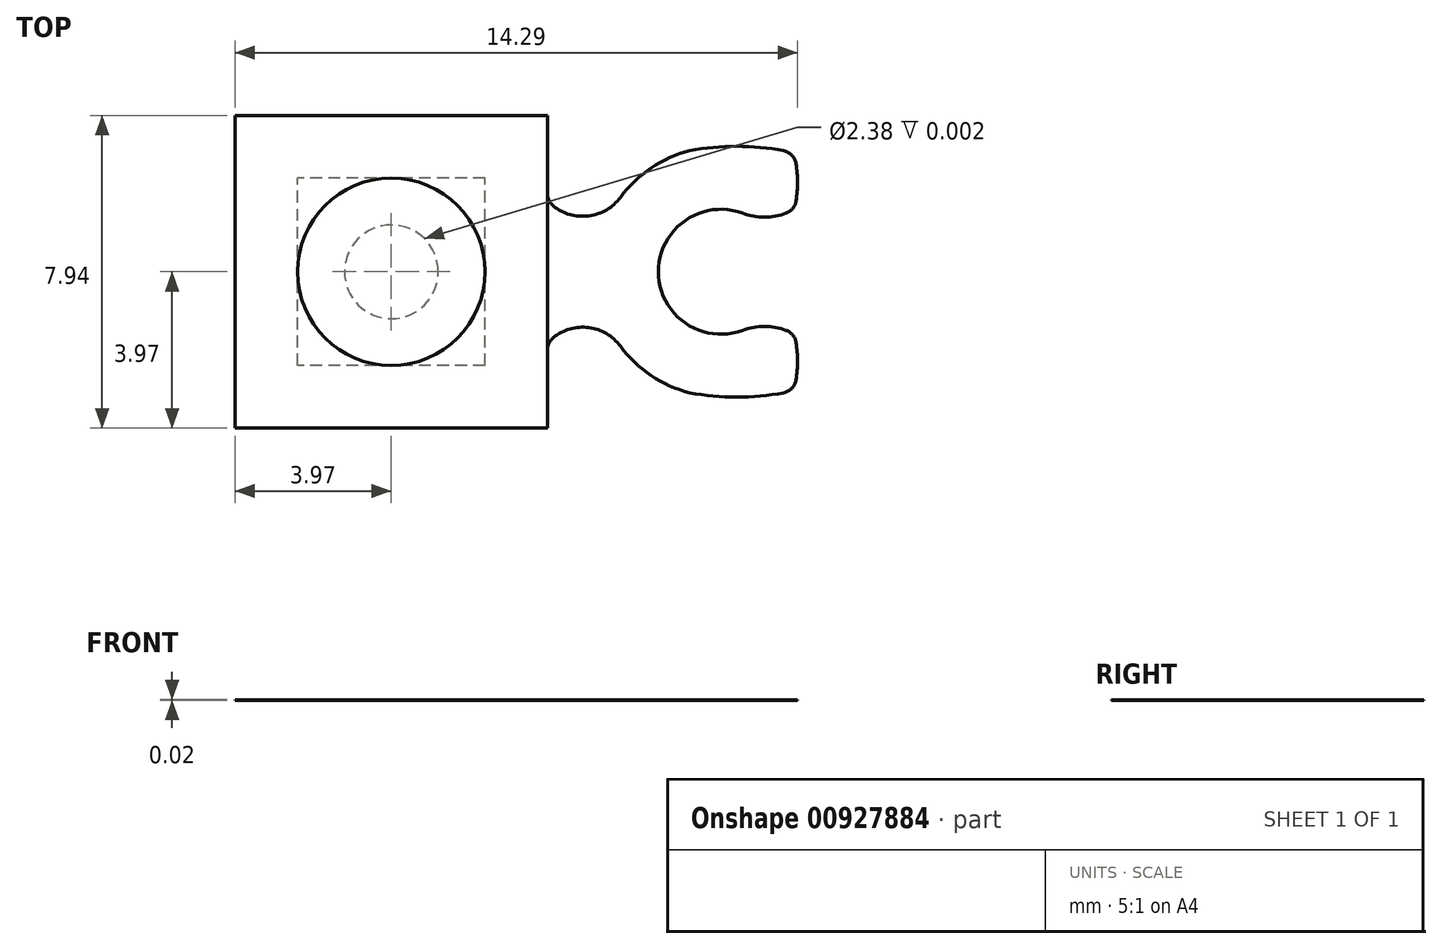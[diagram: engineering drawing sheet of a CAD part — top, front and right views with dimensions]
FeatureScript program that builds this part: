
annotation { "Feature Type Name" : "Feature", "Feature Type Description" : "" }
export const myFeature = defineFeature(function(context is Context, id is Id, definition is map)
    precondition{}
    {
        {
            var Q0;
            Q0=qCreatedBy(makeId("Top.planeOp"),FACE);
            var sketch = newSketch(context, id + "F0", { "sketchPlane" : qUnion([Q0])});
            skLineSegment(sketch, "E0.bottom", {"start": v(3.97, 3.97) * mm, "end": v(-3.97, 3.97) * mm});
            skLineSegment(sketch, "E0.top", {"start": v(3.97, -3.97) * mm, "end": v(-3.97, -3.97) * mm});
            skLineSegment(sketch, "E0.left", {"start": v(3.97, 3.97) * mm, "end": v(3.97, -3.97) * mm});
            skLineSegment(sketch, "E0.right", {"start": v(-3.97, 3.97) * mm, "end": v(-3.97, -3.97) * mm});
            skPoint(sketch, "E0.middle", {"position": v(0, 0) * mm});
            skSolve(sketch);
        }
        {
            var Q0;
            Q0 = qSketchRegion(id + "F0", true);
            extrude(context, id + "F1", {"entities" : qUnion([Q0]), "depth" : 3 / 203.2 * mm, "offsetDistance" : 25.4 * mm});
        }
        {
            var Q0;
            Q0=makeQuery(id+"F1.opExtrude","CAP_FACE",FACE,{"disambiguationData":[OSD([sQuery(id+"F0.wireOp",EDGE,"E0.bottom"),sQuery(id+"F0.wireOp",EDGE,"E0.top"),sQuery(id+"F0.wireOp",EDGE,"E0.left"),sQuery(id+"F0.wireOp",EDGE,"E0.right")])],"isStart":false});
            var sketch = newSketch(context, id + "F2", { "sketchPlane" : qUnion([Q0])});
            skCircle(sketch, "E1", {"center": v(0, 0) * mm, "radius": 2.38 * mm});
            skSolve(sketch);
        }
        {
            var Q0;
            Q0 = qSketchRegion(id + "F2", true);
            extrude(context, id + "F3", {"entities" : qUnion([Q0]), "operationType" : NewBodyOperationType.ADD, "depth" : 1 / 406.4 * mm, "offsetDistance" : 25.4 * mm});
        }
        {
            var Q0;
            Q0=makeQuery(id+"F1.opExtrude","CAP_FACE",FACE,{"disambiguationData":[OSD([sQuery(id+"F0.wireOp",EDGE,"E0.bottom"),sQuery(id+"F0.wireOp",EDGE,"E0.top"),sQuery(id+"F0.wireOp",EDGE,"E0.left"),sQuery(id+"F0.wireOp",EDGE,"E0.right")])],"isStart":false});
            var Q1;
            Q1=makeQuery(id+"F1.opExtrude","CAP_FACE",FACE,{"disambiguationData":[OSD([sQuery(id+"F0.wireOp",EDGE,"E0.bottom"),sQuery(id+"F0.wireOp",EDGE,"E0.top"),sQuery(id+"F0.wireOp",EDGE,"E0.left"),sQuery(id+"F0.wireOp",EDGE,"E0.right")])],"isStart":true});
            cPlane(context, id + "F4", {"entities" : qUnion([Q0, Q1]), "cplaneType" : CPlaneType.MID_PLANE, "offset" : 25.4 * mm, "width" : 152.4 * mm, "height" : 152.4 * mm});
        }
        {
            var Q0;
            Q0=qCreatedBy(id+"F4.planeOp",FACE);
            var sketch = newSketch(context, id + "F5", { "sketchPlane" : qUnion([Q0])});
            skArc(sketch, "E2", {"start": v(8.92, 1.49) * mm, "mid": v(7.47, 1.3) * mm, "end": v(6.78, 0) * mm});
            skLineSegment(sketch, "E3", {"start": v(0, 0) * mm, "end": v(12.83, 0) * mm, "construction": true});
            skArc(sketch, "E4", {"start": v(4.12, 1.67) * mm, "mid": v(5.01, 1.42) * mm, "end": v(5.82, 1.9) * mm});
            skArc(sketch, "E5", {"start": v(7.58, 3.08) * mm, "mid": v(6.6, 2.63) * mm, "end": v(5.82, 1.9) * mm});
            skArc(sketch, "E6", {"start": v(3.97, 1.98) * mm, "mid": v(4, 1.81) * mm, "end": v(4.12, 1.67) * mm});
            skLineSegment(sketch, "E7", {"start": v(3.97, 0) * mm, "end": v(3.97, 1.98) * mm});
            skArc(sketch, "E8", {"start": v(8.92, 1.49) * mm, "mid": v(9.48, 1.39) * mm, "end": v(10.03, 1.49) * mm});
            skArc(sketch, "E9", {"start": v(10.03, 1.49) * mm, "mid": v(10.2, 1.61) * mm, "end": v(10.28, 1.8) * mm});
            skArc(sketch, "E10", {"start": v(10.28, 1.8) * mm, "mid": v(10.32, 2.27) * mm, "end": v(10.28, 2.74) * mm});
            skArc(sketch, "E11", {"start": v(10.28, 2.74) * mm, "mid": v(10.18, 2.96) * mm, "end": v(9.97, 3.08) * mm});
            skArc(sketch, "E12.trimOffspring", {"start": v(9.97, 3.08) * mm, "mid": v(8.77, 3.19) * mm, "end": v(7.58, 3.08) * mm});
            skArc(sketch, "E13.MirrorCS", {"start": v(8.92, -1.49) * mm, "mid": v(7.47, -1.3) * mm, "end": v(6.78, 0) * mm});
            skArc(sketch, "E14.MirrorCS", {"start": v(10.28, -1.8) * mm, "mid": v(10.32, -2.27) * mm, "end": v(10.28, -2.74) * mm});
            skLineSegment(sketch, "E15.MirrorCS", {"start": v(3.97, 0) * mm, "end": v(3.97, -1.98) * mm});
            skArc(sketch, "E16.MirrorCS", {"start": v(8.92, -1.49) * mm, "mid": v(9.48, -1.39) * mm, "end": v(10.03, -1.49) * mm});
            skArc(sketch, "E17.MirrorCS", {"start": v(4.12, -1.67) * mm, "mid": v(5.01, -1.42) * mm, "end": v(5.82, -1.9) * mm});
            skArc(sketch, "E18.MirrorCS", {"start": v(10.28, -2.74) * mm, "mid": v(10.18, -2.96) * mm, "end": v(9.97, -3.08) * mm});
            skArc(sketch, "E19.MirrorCS", {"start": v(7.58, -3.08) * mm, "mid": v(6.6, -2.63) * mm, "end": v(5.82, -1.9) * mm});
            skArc(sketch, "E20.MirrorCS", {"start": v(3.97, -1.98) * mm, "mid": v(4, -1.81) * mm, "end": v(4.12, -1.67) * mm});
            skArc(sketch, "E21.MirrorCS", {"start": v(9.97, -3.08) * mm, "mid": v(8.77, -3.19) * mm, "end": v(7.58, -3.08) * mm});
            skArc(sketch, "E22.MirrorCS", {"start": v(10.03, -1.49) * mm, "mid": v(10.2, -1.61) * mm, "end": v(10.28, -1.8) * mm});
            skSolve(sketch);
        }
        {
            var Q0;
            Q0 = qSketchRegion(id + "F5", true);
            extrude(context, id + "F6", {"entities" : qUnion([Q0]), "operationType" : NewBodyOperationType.ADD, "depth" : 1 / 203.2 * mm, "offsetDistance" : 25.4 * mm, "symmetric" : true});
        }
        {
            var Q0;
            Q0=makeQuery(id+"F1.opExtrude","CAP_FACE",FACE,{"disambiguationData":[OSD([sQuery(id+"F0.wireOp",EDGE,"E0.bottom"),sQuery(id+"F0.wireOp",EDGE,"E0.top"),sQuery(id+"F0.wireOp",EDGE,"E0.left"),sQuery(id+"F0.wireOp",EDGE,"E0.right")])],"isStart":true});
            var sketch = newSketch(context, id + "F7", { "sketchPlane" : qUnion([Q0])});
            skLineSegment(sketch, "E23.bottom", {"start": v(2.38, 2.38) * mm, "end": v(-2.38, 2.38) * mm});
            skLineSegment(sketch, "E23.top", {"start": v(2.38, -2.38) * mm, "end": v(-2.38, -2.38) * mm});
            skLineSegment(sketch, "E23.left", {"start": v(2.38, 2.38) * mm, "end": v(2.38, -2.38) * mm});
            skLineSegment(sketch, "E23.right", {"start": v(-2.38, 2.38) * mm, "end": v(-2.38, -2.38) * mm});
            skPoint(sketch, "E23.middle", {"position": v(0, 0) * mm});
            skSolve(sketch);
        }
        {
            var Q0;
            Q0 = qSketchRegion(id + "F7", true);
            var Q1;
            Q1=makeQuery(id+"F1.opExtrude","CAP_FACE",FACE,{"disambiguationData":[OSD([sQuery(id+"F0.wireOp",EDGE,"E0.bottom"),sQuery(id+"F0.wireOp",EDGE,"E0.top"),sQuery(id+"F0.wireOp",EDGE,"E0.left"),sQuery(id+"F0.wireOp",EDGE,"E0.right")])],"isStart":false});
            extrude(context, id + "F8", {"entities" : qUnion([Q0]), "operationType" : NewBodyOperationType.REMOVE, "endBound" : BoundingType.UP_TO_SURFACE, "oppositeDirection" : true, "depth" : 25.4 * mm, "endBoundEntityFace" : qUnion([Q1]), "hasOffset" : true, "offsetDistance" : 1 / 406.4 * mm});
        }
        {
            var Q0;
            Q0=makeQuery(id+"F8.boolean.opBoolean","COPY",FACE,{"derivedFrom":makeQuery(id+"F8.opExtrude","CAP_FACE",FACE,{"disambiguationData":[OSD([sQuery(id+"F7.wireOp",EDGE,"E23.bottom"),sQuery(id+"F7.wireOp",EDGE,"E23.top"),sQuery(id+"F7.wireOp",EDGE,"E23.left"),sQuery(id+"F7.wireOp",EDGE,"E23.right")])],"isStart":false})});
            var sketch = newSketch(context, id + "F9", { "sketchPlane" : qUnion([Q0])});
            skCircle(sketch, "E24", {"center": v(0, 0) * mm, "radius": 1.2 * mm});
            skSolve(sketch);
        }
        {
            var Q0;
            Q0=makeQuery(id+"F9.imprint","IMPRINT",FACE,{"disambiguationData":[TD([[makeQuery(id+"F9.imprint","IMPRINT",EDGE,{"derivedFrom":sQuery(id+"F9.wireOp",EDGE,"E24")}),1.0]])]});
            extrude(context, id + "F10", {"entities" : qUnion([Q0]), "operationType" : NewBodyOperationType.REMOVE, "oppositeDirection" : true, "depth" : 1 / 406.4 * mm, "offsetDistance" : 25.4 * mm});
        }
    });
